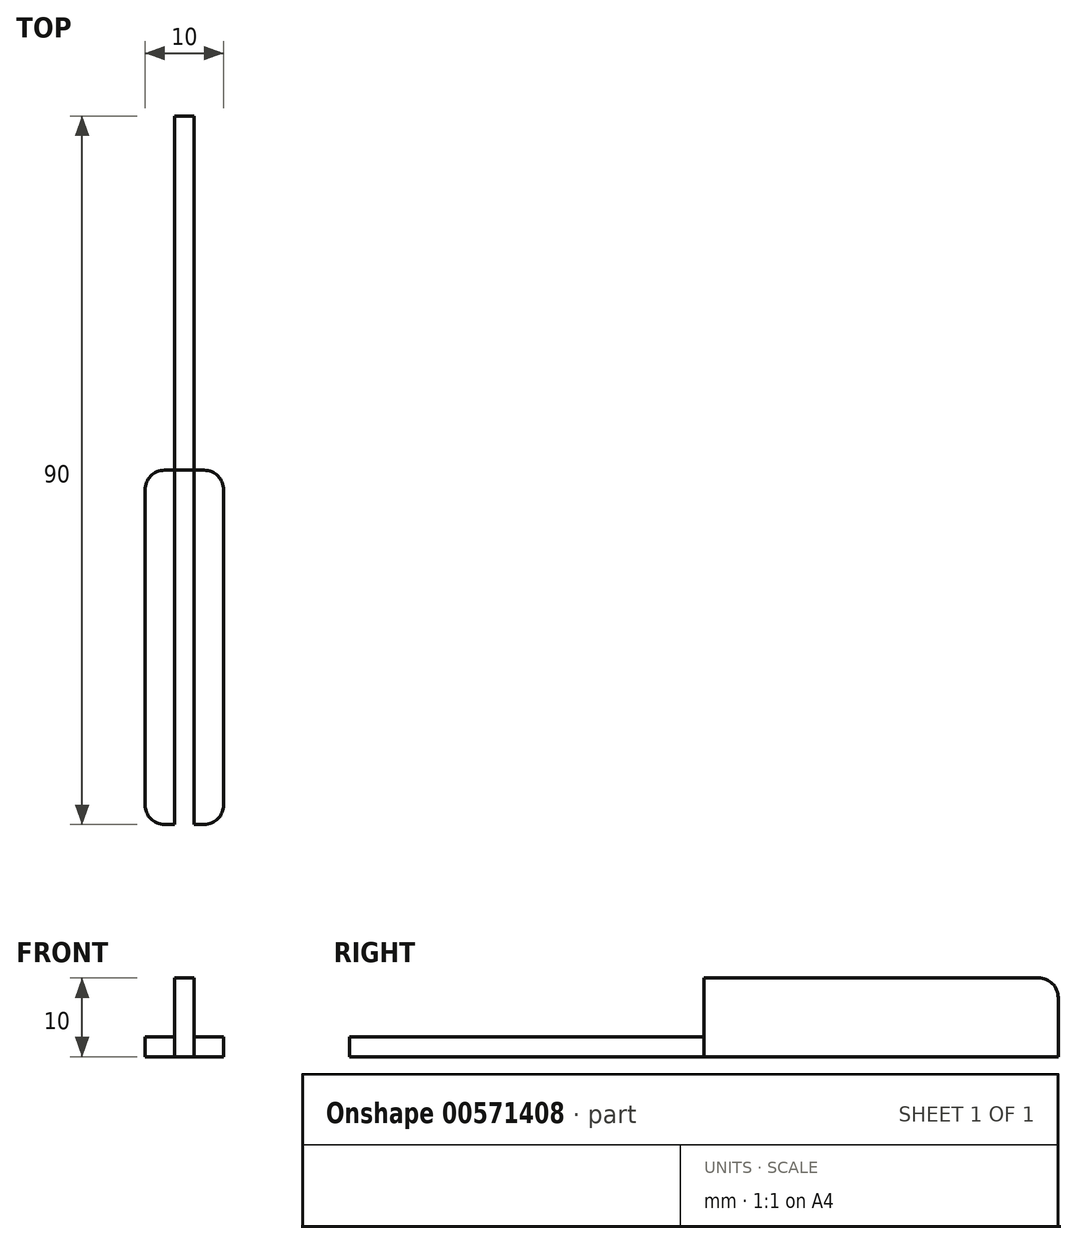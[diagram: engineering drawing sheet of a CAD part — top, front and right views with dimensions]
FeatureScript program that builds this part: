
annotation { "Feature Type Name" : "Feature", "Feature Type Description" : "" }
export const myFeature = defineFeature(function(context is Context, id is Id, definition is map)
    precondition{}
    {
        {
            var Q0;
            Q0=qCreatedBy(makeId("Top.planeOp"),FACE);
            var sketch = newSketch(context, id + "F0", { "sketchPlane" : qUnion([Q0])});
            skLineSegment(sketch, "E0.bottom", {"start": v(5, 22.5) * mm, "end": v(-5, 22.5) * mm});
            skLineSegment(sketch, "E0.top", {"start": v(5, -22.5) * mm, "end": v(-5, -22.5) * mm});
            skLineSegment(sketch, "E0.left", {"start": v(5, 22.5) * mm, "end": v(5, -22.5) * mm});
            skLineSegment(sketch, "E0.right", {"start": v(-5, 22.5) * mm, "end": v(-5, -22.5) * mm});
            skPoint(sketch, "E0.middle", {"position": v(0, 0) * mm});
            skLineSegment(sketch, "E1.bottom", {"start": v(0, -22.5) * mm, "end": v(1.25, -22.5) * mm});
            skLineSegment(sketch, "E1.top", {"start": v(0, 67.5) * mm, "end": v(1.25, 67.5) * mm});
            skLineSegment(sketch, "E1.left", {"start": v(0, -22.5) * mm, "end": v(0, 67.5) * mm});
            skLineSegment(sketch, "E1.right", {"start": v(1.25, -22.5) * mm, "end": v(1.25, 67.5) * mm});
            skLineSegment(sketch, "E2.bottom", {"start": v(0, -22.5) * mm, "end": v(-1.25, -22.5) * mm});
            skLineSegment(sketch, "E2.top", {"start": v(0, 67.5) * mm, "end": v(-1.25, 67.5) * mm});
            skLineSegment(sketch, "E2.right", {"start": v(-1.25, -22.5) * mm, "end": v(-1.25, 67.5) * mm});
            skSolve(sketch);
        }
        {
            var Q0;
            {var subQ5=sQuery(id+"F0.wireOp",EDGE,"E2.top");Q0=makeQuery(id+"F0.imprint","IMPRINT",FACE,{"disambiguationData":[TD([[makeQuery(id+"F0.imprint","IMPRINT",EDGE,{"derivedFrom":subQ5}),1.0]])]});}
            var Q1;
            {var subQ5=sQuery(id+"F0.wireOp",EDGE,"E1.top");Q1=makeQuery(id+"F0.imprint","IMPRINT",FACE,{"disambiguationData":[TD([[makeQuery(id+"F0.imprint","IMPRINT",EDGE,{"derivedFrom":subQ5}),-1.0]])]});}
            var Q2;
            {var subQ5=sQuery(id+"F0.wireOp",EDGE,"E2.bottom");Q2=makeQuery(id+"F0.imprint","IMPRINT",FACE,{"disambiguationData":[TD([[makeQuery(id+"F0.imprint","IMPRINT",EDGE,{"derivedFrom":subQ5}),-1.0]])]});}
            var Q3;
            {var subQ5=sQuery(id+"F0.wireOp",EDGE,"E1.bottom");Q3=makeQuery(id+"F0.imprint","IMPRINT",FACE,{"disambiguationData":[TD([[makeQuery(id+"F0.imprint","IMPRINT",EDGE,{"derivedFrom":subQ5}),1.0]])]});}
            extrude(context, id + "F1", {"entities" : qUnion([Q0, Q1, Q2, Q3]), "depth" : 10 * mm, "offsetDistance" : 25 * mm});
        }
        {
            var Q0;
            {var subQ0=sQuery(id+"F0.wireOp",EDGE,"E0.left");Q0=makeQuery(id+"F0.imprint","IMPRINT",FACE,{"disambiguationData":[TD([[makeQuery(id+"F0.imprint","IMPRINT",EDGE,{"derivedFrom":subQ0}),-1.0]])]});}
            var Q1;
            {var subQ0=sQuery(id+"F0.wireOp",EDGE,"E0.right");Q1=makeQuery(id+"F0.imprint","IMPRINT",FACE,{"disambiguationData":[TD([[makeQuery(id+"F0.imprint","IMPRINT",EDGE,{"derivedFrom":subQ0}),1.0]])]});}
            var Q2;
            {var subQ5=sQuery(id+"F0.wireOp",EDGE,"E1.bottom");Q2=makeQuery(id+"F0.imprint","IMPRINT",FACE,{"disambiguationData":[TD([[makeQuery(id+"F0.imprint","IMPRINT",EDGE,{"derivedFrom":subQ5}),1.0]])]});}
            var Q3;
            {var subQ5=sQuery(id+"F0.wireOp",EDGE,"E2.bottom");Q3=makeQuery(id+"F0.imprint","IMPRINT",FACE,{"disambiguationData":[TD([[makeQuery(id+"F0.imprint","IMPRINT",EDGE,{"derivedFrom":subQ5}),-1.0]])]});}
            extrude(context, id + "F2", {"entities" : qUnion([Q0, Q1, Q2, Q3]), "operationType" : NewBodyOperationType.ADD, "depth" : 2.5 * mm, "offsetDistance" : 25 * mm});
        }
        {
            var Q0;
            Q0=makeQuery(id+"F2.opExtrude","SWEPT_EDGE",EDGE,{"disambiguationData":[OSD([sQuery(id+"F0.wireOp",EDGE,"E0.bottom"),sQuery(id+"F0.wireOp",EDGE,"E0.left")])]});
            var Q1;
            Q1=makeQuery(id+"F2.opExtrude","SWEPT_EDGE",EDGE,{"disambiguationData":[OSD([sQuery(id+"F0.wireOp",EDGE,"E0.bottom"),sQuery(id+"F0.wireOp",EDGE,"E0.right")])]});
            var Q2;
            Q2=makeQuery(id+"F2.opExtrude","SWEPT_EDGE",EDGE,{"disambiguationData":[OSD([sQuery(id+"F0.wireOp",EDGE,"E0.top"),sQuery(id+"F0.wireOp",EDGE,"E0.right")])]});
            var Q3;
            Q3=makeQuery(id+"F2.opExtrude","SWEPT_EDGE",EDGE,{"disambiguationData":[OSD([sQuery(id+"F0.wireOp",EDGE,"E0.top"),sQuery(id+"F0.wireOp",EDGE,"E0.left")])]});
            fillet(context, id + "F3", {"entities" : qUnion([Q0, Q1, Q2, Q3]), "radius" : 2.5 * mm, "tangentPropagation" : true, "allowEdgeOverflow" : false});
        }
        {
            var Q0;
            Q0=makeQuery(id+"F1.opExtrude","CAP_EDGE",EDGE,{"disambiguationData":[OSD([sQuery(id+"F0.wireOp",EDGE,"E1.bottom"),sQuery(id+"F0.wireOp",EDGE,"E2.bottom")])],"isStart":false});
            var Q1;
            Q1=makeQuery(id+"F1.opExtrude","CAP_EDGE",EDGE,{"disambiguationData":[OSD([sQuery(id+"F0.wireOp",EDGE,"E1.top"),sQuery(id+"F0.wireOp",EDGE,"E2.top")])],"isStart":false});
            fillet(context, id + "F4", {"entities" : qUnion([Q0, Q1]), "radius" : 2.5 * mm, "tangentPropagation" : true, "allowEdgeOverflow" : false});
        }
    });
